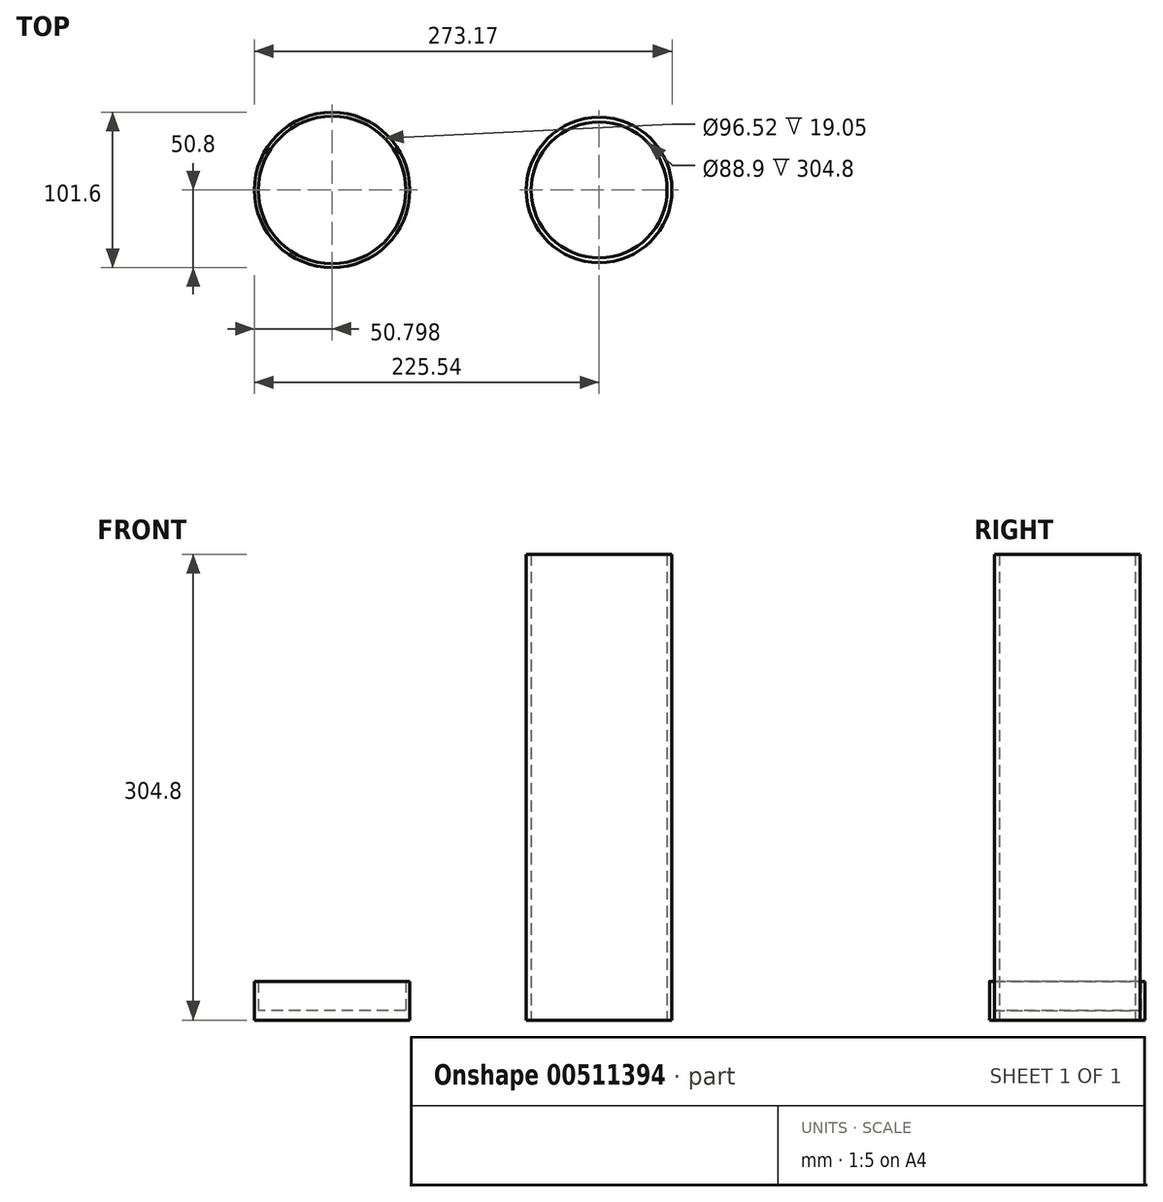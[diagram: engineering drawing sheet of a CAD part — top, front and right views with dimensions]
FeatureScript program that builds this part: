
annotation { "Feature Type Name" : "Feature", "Feature Type Description" : "" }
export const myFeature = defineFeature(function(context is Context, id is Id, definition is map)
    precondition{}
    {
        {
            var Q0;
            Q0=qCreatedBy(makeId("Top.planeOp"),FACE);
            var sketch = newSketch(context, id + "F0", { "sketchPlane" : qUnion([Q0])});
            skCircle(sketch, "E0", {"center": v(0, 0) * mm, "radius": 44.45 * mm});
            skCircle(sketch, "E1", {"center": v(0, 0) * mm, "radius": 47.63 * mm});
            skCircle(sketch, "E2", {"center": v(-174.74, 0) * mm, "radius": 48.26 * mm});
            skCircle(sketch, "E3", {"center": v(-174.74, 0) * mm, "radius": 50.8 * mm});
            skSolve(sketch);
        }
        {
            var Q0;
            Q0=makeQuery(id+"F0.imprint","IMPRINT",FACE,{"disambiguationData":[TD([[makeQuery(id+"F0.imprint","IMPRINT",EDGE,{"derivedFrom":sQuery(id+"F0.wireOp",EDGE,"E0")}),-1.0]])]});
            extrude(context, id + "F1", {"entities" : qUnion([Q0]), "depth" : 304.8 * mm});
        }
        {
            var Q0;
            Q0=makeQuery(id+"F0.imprint","IMPRINT",FACE,{"disambiguationData":[TD([[makeQuery(id+"F0.imprint","IMPRINT",EDGE,{"derivedFrom":sQuery(id+"F0.wireOp",EDGE,"E2")}),1.0]])]});
            extrude(context, id + "F2", {"entities" : qUnion([Q0]), "depth" : 6.35 * mm});
        }
        {
            var Q0;
            Q0=makeQuery(id+"F0.imprint","IMPRINT",FACE,{"disambiguationData":[TD([[makeQuery(id+"F0.imprint","IMPRINT",EDGE,{"derivedFrom":sQuery(id+"F0.wireOp",EDGE,"E2")}),-1.0]])]});
            extrude(context, id + "F3", {"entities" : qUnion([Q0]), "operationType" : NewBodyOperationType.ADD, "depth" : 25.4 * mm});
        }
    });
